# Revit family: 1802a_lvseries
name_source: partatom
category: Communication Devices
revit_build: Autodesk Revit 2014 (Build: 20130308_1515(x64)
units: mm (PartAtom-declared; Revit-internal decimal feet)

## types (2) — shared parameters
Assembly Code = D5090
Black = Paint - Hubbell - Carbon Black
Default Elevation = 48 "
Description = Our Low Voltage Wall Switches are designed for virtually any
area. The soft contours of its architecturally-pleasing design fit
easily into any décor. Momentary version switches are available
and feature multiple button configurations making them the
perfect switch solution for low voltage occupancy sensors,
daylighting controls and networked lighting control panels.
Features = Attractive, architecturally pleasing design
• Momentary or latching button action
• 1-4 buttons with or without LED
• Mounts to standard single-gang box
• California Title 24 compliant
• Five-year limited warranty
• Low voltage device: 24VDC
Height = 4.5 "
Manufacturer = Hubbell Control Solutions
Model = Low Voltage Switches
Product Documentation Link = https://hubbellcdn.com
Product Page URL = https://www.hubbell.com
Type Comments = Low Voltage Switches
URL = https://www.hubbell.com
Warranty = 5-Years Warranty
White = Paint - Hubbell - Matte White
Width = 2.75 "

## per-type parameters (varying)
| type | LED |
| LVSM1NP | No |
| LVSM1PL | Yes |

## geometry (parser evidence)
native form markers: Sweep x1
no freeform markers — native parametric forms only
